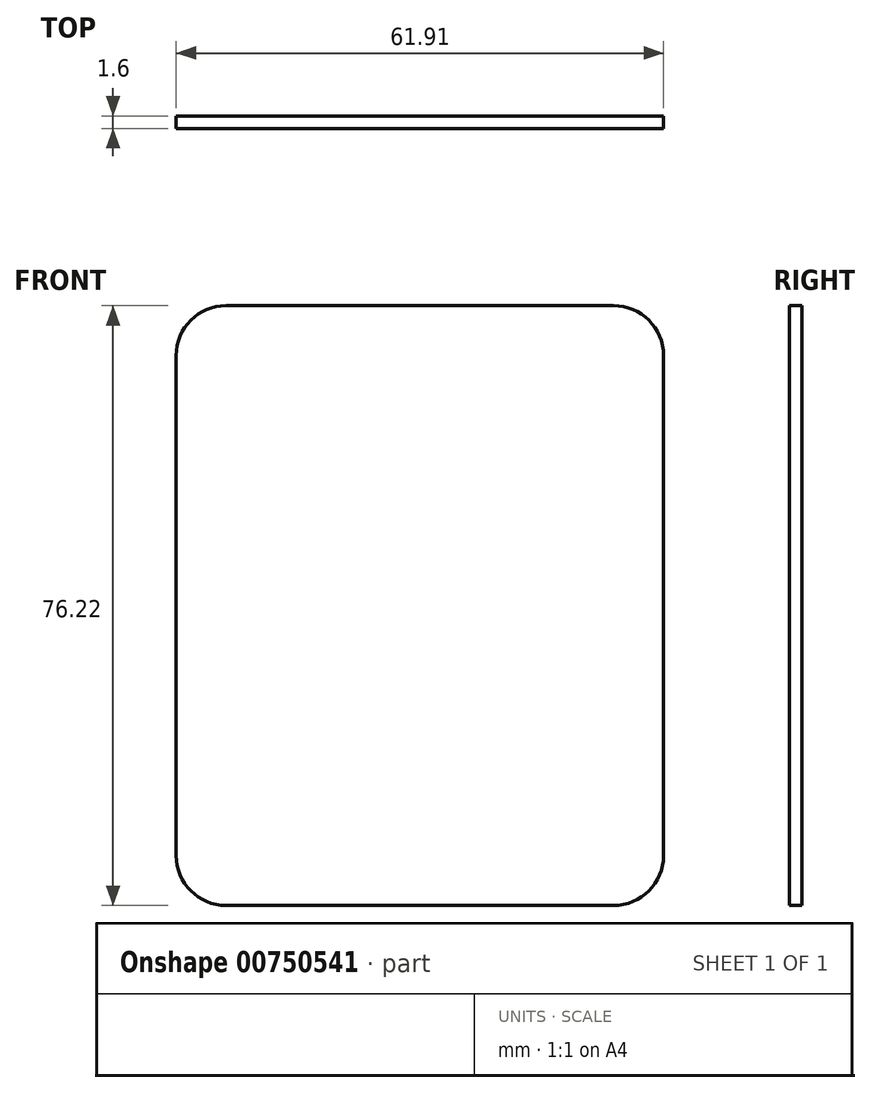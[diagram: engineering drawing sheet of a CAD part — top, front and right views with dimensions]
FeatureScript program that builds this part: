
annotation { "Feature Type Name" : "Feature", "Feature Type Description" : "" }
export const myFeature = defineFeature(function(context is Context, id is Id, definition is map)
    precondition{}
    {
        {
            var Q0;
            Q0=qCreatedBy(makeId("Front.planeOp"),FACE);
            var sketch = newSketch(context, id + "F0", { "sketchPlane" : qUnion([Q0])});
            skLineSegment(sketch, "E0.bottom", {"start": v(-24.46, 29.64) * mm, "end": v(24.75, 29.64) * mm});
            skLineSegment(sketch, "E0.top", {"start": v(-24.46, -46.58) * mm, "end": v(24.75, -46.58) * mm});
            skLineSegment(sketch, "E0.left", {"start": v(-30.8, 23.29) * mm, "end": v(-30.8, -40.23) * mm});
            skLineSegment(sketch, "E0.right", {"start": v(31.1, 23.29) * mm, "end": v(31.1, -40.23) * mm});
            skPoint(sketch, "E1.visualSharp", {"position": v(-30.8, 29.64) * mm});
            skArc(sketch, "E1.filletArc", {"start": v(-24.46, 29.64) * mm, "mid": v(-28.95, 27.78) * mm, "end": v(-30.8, 23.29) * mm});
            skPoint(sketch, "E2.visualSharp", {"position": v(31.1, 29.64) * mm});
            skArc(sketch, "E2.filletArc", {"start": v(31.1, 23.29) * mm, "mid": v(29.24, 27.78) * mm, "end": v(24.75, 29.64) * mm});
            skPoint(sketch, "E3.visualSharp", {"position": v(31.1, -46.58) * mm});
            skArc(sketch, "E3.filletArc", {"start": v(24.75, -46.58) * mm, "mid": v(29.24, -44.72) * mm, "end": v(31.1, -40.23) * mm});
            skPoint(sketch, "E4.visualSharp", {"position": v(-30.8, -46.58) * mm});
            skArc(sketch, "E4.filletArc", {"start": v(-30.8, -40.23) * mm, "mid": v(-28.95, -44.72) * mm, "end": v(-24.46, -46.58) * mm});
            skSolve(sketch);
        }
        {
            var Q0;
            Q0 = qSketchRegion(id + "F0", true);
            extrude(context, id + "F1", {"entities" : qUnion([Q0]), "depth" : 1.6 * mm, "offsetDistance" : 25.4 * mm});
        }
    });
